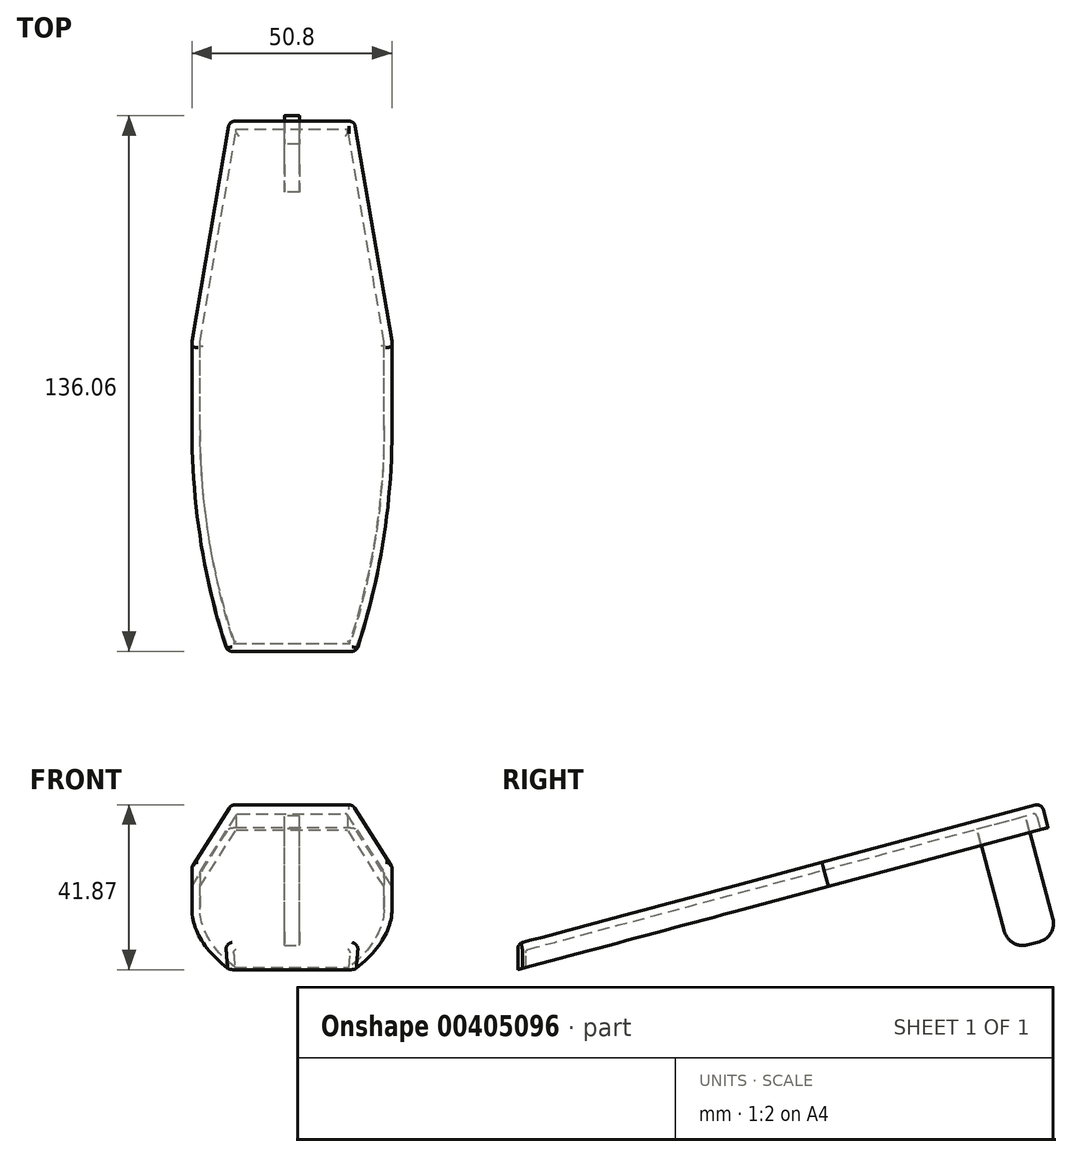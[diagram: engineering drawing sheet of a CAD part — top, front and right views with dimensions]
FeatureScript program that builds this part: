
annotation { "Feature Type Name" : "Feature", "Feature Type Description" : "" }
export const myFeature = defineFeature(function(context is Context, id is Id, definition is map)
    precondition{}
    {
        {
            var Q0;
            Q0=qCreatedBy(makeId("Right.planeOp"),FACE);
            var sketch = newSketch(context, id + "F0", { "sketchPlane" : qUnion([Q0])});
            skLineSegment(sketch, "E0", {"start": v(3.05, 2.38) * mm, "end": v(91.05, 71.15) * mm});
            skLineSegment(sketch, "E1", {"start": v(91.05, 71.15) * mm, "end": v(74.61, 132.48) * mm, "construction": true});
            skLineSegment(sketch, "E2", {"start": v(74.61, 132.48) * mm, "end": v(-60.33, 96.33) * mm});
            skLineSegment(sketch, "E3", {"start": v(-60.32, 96.33) * mm, "end": v(-60.33, -5.27) * mm});
            skLineSegment(sketch, "E4", {"start": v(-60.33, -5.27) * mm, "end": v(-7.85, -39.35) * mm});
            skLineSegment(sketch, "E5", {"start": v(0, -35.1) * mm, "end": v(0, -3.87) * mm});
            skPoint(sketch, "E6.visualSharp", {"position": v(0, 0) * mm});
            skArc(sketch, "E6.filletArc", {"start": v(3.05, 2.38) * mm, "mid": v(0.8, -0.4) * mm, "end": v(0, -3.87) * mm});
            skPoint(sketch, "E7.visualSharp", {"position": v(0, -44.45) * mm});
            skArc(sketch, "E7.filletArc", {"start": v(-7.85, -39.35) * mm, "mid": v(-2.66, -39.56) * mm, "end": v(0, -35.1) * mm});
            skArc(sketch, "E8", {"start": v(83.71, 98.52) * mm, "mid": v(82.28, 88.61) * mm, "end": v(88.48, 80.74) * mm});
            skCircle(sketch, "E9", {"center": v(69.86, 113.43) * mm, "radius": 3.18 * mm});
            skLineSegment(sketch, "E10", {"start": v(74.61, 132.48) * mm, "end": v(83.71, 98.52) * mm});
            skLineSegment(sketch, "E11", {"start": v(88.48, 80.74) * mm, "end": v(91.05, 71.15) * mm});
            skLineSegment(sketch, "E12", {"start": v(74.61, 132.48) * mm, "end": v(94.34, 58.88) * mm, "construction": true});
            skLineSegment(sketch, "E13", {"start": v(-60.33, 96.33) * mm, "end": v(-60.33, -44.45) * mm, "construction": true});
            skLineSegment(sketch, "E14", {"start": v(74.61, 132.48) * mm, "end": v(122.02, -44.45) * mm, "construction": true});
            skLineSegment(sketch, "E15", {"start": v(-60.33, -44.45) * mm, "end": v(122.02, -44.45) * mm, "construction": true});
            skSolve(sketch);
        }
        {
            var Q0;
            Q0=sQuery(id+"F0.wireOp",EDGE,"E2");
            cPlane(context, id + "F1", {"entities" : qUnion([Q0]), "cplaneType" : CPlaneType.LINE_ANGLE, "offset" : 25.4 * mm, "angle" : 0 * degree, "width" : 152.4 * mm, "height" : 152.4 * mm});
        }
        {
            var Q0;
            Q0=qCreatedBy(id+"F1.planeOp",FACE);
            var sketch = newSketch(context, id + "F2", { "sketchPlane" : qUnion([Q0])});
            skLineSegment(sketch, "E16.0", {"start": v(0, -106.36) * mm, "end": v(0, 33.34) * mm, "construction": true});
            skLineSegment(sketch, "E17", {"start": v(0, 33.34) * mm, "end": v(15.88, 33.34) * mm});
            skLineSegment(sketch, "E18", {"start": v(15.88, 33.34) * mm, "end": v(25.4, -26.15) * mm, "construction": true});
            skLineSegment(sketch, "E19", {"start": v(25.4, -26.15) * mm, "end": v(25.4, -48.6) * mm});
            skArc(sketch, "E20", {"start": v(25.4, -26.15) * mm, "mid": v(23, 3.98) * mm, "end": v(15.88, 33.34) * mm});
            skLineSegment(sketch, "E21", {"start": v(25.4, -48.6) * mm, "end": v(15.88, -106.36) * mm});
            skLineSegment(sketch, "E22", {"start": v(15.88, -106.36) * mm, "end": v(0, -106.36) * mm});
            skLineSegment(sketch, "E23.MirrorCS", {"start": v(0, 33.34) * mm, "end": v(-15.88, 33.34) * mm});
            skArc(sketch, "E24.MirrorCS", {"start": v(-25.4, -26.15) * mm, "mid": v(-23, 3.98) * mm, "end": v(-15.88, 33.34) * mm});
            skLineSegment(sketch, "E25.MirrorCS", {"start": v(-25.4, -26.15) * mm, "end": v(-25.4, -48.6) * mm});
            skLineSegment(sketch, "E26.MirrorCS", {"start": v(-25.4, -48.6) * mm, "end": v(-15.88, -106.36) * mm});
            skLineSegment(sketch, "E27.MirrorCS", {"start": v(-15.88, -106.36) * mm, "end": v(0, -106.36) * mm});
            skSolve(sketch);
        }
        {
            var Q0;
            Q0=makeQuery(id+"F2.imprint","IMPRINT",FACE,{"disambiguationData":[TD([[makeQuery(id+"F2.imprint","IMPRINT",EDGE,{"derivedFrom":sQuery(id+"F2.wireOp",EDGE,"E17")}),-1.0]])]});
            extrude(context, id + "F3", {"entities" : qUnion([Q0]), "oppositeDirection" : true, "depth" : 6.35 * mm, "offsetDistance" : 25.4 * mm});
        }
        {
            var Q0;
            Q0=qCreatedBy(makeId("Right.planeOp"),FACE);
            var sketch = newSketch(context, id + "F4", { "sketchPlane" : qUnion([Q0])});
            skLineSegment(sketch, "E28.0", {"start": v(-61.97, 102.46) * mm, "end": v(-60.33, 96.33) * mm});
            skLineSegment(sketch, "E28.1", {"start": v(-4.51, 117.85) * mm, "end": v(-61.97, 102.46) * mm, "construction": true});
            skLineSegment(sketch, "E29", {"start": v(-61.97, 102.46) * mm, "end": v(-60.08, 102.97) * mm});
            skLineSegment(sketch, "E30", {"start": v(-60.08, 102.97) * mm, "end": v(-60.08, 96.4) * mm});
            skLineSegment(sketch, "E31", {"start": v(-60.08, 96.4) * mm, "end": v(-60.33, 96.33) * mm});
            skSolve(sketch);
        }
        {
            var Q0;
            Q0 = qSketchRegion(id + "F4", true);
            extrude(context, id + "F5", {"entities" : qUnion([Q0]), "operationType" : NewBodyOperationType.REMOVE, "endBound" : BoundingType.THROUGH_ALL, "oppositeDirection" : true, "depth" : 25.4 * mm, "offsetDistance" : 25.4 * mm, "hasSecondDirection" : true, "secondDirectionBound" : SecondDirectionBoundingType.THROUGH_ALL, "secondDirectionOppositeDirection" : false, "secondDirectionDepth" : 25.4 * mm});
        }
        {
            var Q0;
            Q0=makeQuery(id+"F3.opExtrude","CAP_FACE",FACE,{"disambiguationData":[OSD([sQuery(id+"F2.wireOp",EDGE,"E17"),sQuery(id+"F2.wireOp",EDGE,"E19"),sQuery(id+"F2.wireOp",EDGE,"E20"),sQuery(id+"F2.wireOp",EDGE,"E21"),sQuery(id+"F2.wireOp",EDGE,"E22"),sQuery(id+"F2.wireOp",EDGE,"E23.MirrorCS"),sQuery(id+"F2.wireOp",EDGE,"E24.MirrorCS"),sQuery(id+"F2.wireOp",EDGE,"E25.MirrorCS"),sQuery(id+"F2.wireOp",EDGE,"E26.MirrorCS"),sQuery(id+"F2.wireOp",EDGE,"E27.MirrorCS")])],"isStart":true});
            shell(context, id + "F6", {"entities" : qUnion([Q0]), "thickness" : 2.03 * mm});
        }
        {
            var Q0;
            Q0=makeQuery(id+"F3.opExtrude","SWEPT_EDGE",EDGE,{"disambiguationData":[OSD([sQuery(id+"F2.wireOp",EDGE,"E17"),sQuery(id+"F2.wireOp",EDGE,"E20")])]});
            var Q1;
            Q1=makeQuery(id+"F3.opExtrude","SWEPT_EDGE",EDGE,{"disambiguationData":[OSD([sQuery(id+"F2.wireOp",EDGE,"E23.MirrorCS"),sQuery(id+"F2.wireOp",EDGE,"E24.MirrorCS")])]});
            var Q2;
            Q2=makeQuery(id+"F3.opExtrude","SWEPT_EDGE",EDGE,{"disambiguationData":[OSD([sQuery(id+"F2.wireOp",EDGE,"E21"),sQuery(id+"F2.wireOp",EDGE,"E22")])]});
            var Q3;
            Q3=makeQuery(id+"F3.opExtrude","SWEPT_EDGE",EDGE,{"disambiguationData":[OSD([sQuery(id+"F2.wireOp",EDGE,"E26.MirrorCS"),sQuery(id+"F2.wireOp",EDGE,"E27.MirrorCS")])]});
            var Q4;
            Q4=makeQuery(id+"F3.opExtrude","CAP_FACE",FACE,{"disambiguationData":[OSD([sQuery(id+"F2.wireOp",EDGE,"E17"),sQuery(id+"F2.wireOp",EDGE,"E19"),sQuery(id+"F2.wireOp",EDGE,"E20"),sQuery(id+"F2.wireOp",EDGE,"E21"),sQuery(id+"F2.wireOp",EDGE,"E22"),sQuery(id+"F2.wireOp",EDGE,"E23.MirrorCS"),sQuery(id+"F2.wireOp",EDGE,"E24.MirrorCS"),sQuery(id+"F2.wireOp",EDGE,"E25.MirrorCS"),sQuery(id+"F2.wireOp",EDGE,"E26.MirrorCS"),sQuery(id+"F2.wireOp",EDGE,"E27.MirrorCS")])],"isStart":false});
            var Q5;
            Q5=makeQuery(id+"F5.boolean.opBoolean","INTERSECT",EDGE,{"derivedFrom":[makeQuery(id+"F3.opExtrude","SWEPT_FACE",FACE,{"disambiguationData":[OSD([sQuery(id+"F2.wireOp",EDGE,"E20")])]}),makeQuery(id+"F5.opExtrude","SWEPT_FACE",FACE,{"disambiguationData":[OSD([sQuery(id+"F4.wireOp",EDGE,"E30")])]})]});
            var Q6;
            Q6=makeQuery(id+"F5.boolean.opBoolean","INTERSECT",EDGE,{"derivedFrom":[makeQuery(id+"F3.opExtrude","SWEPT_FACE",FACE,{"disambiguationData":[OSD([sQuery(id+"F2.wireOp",EDGE,"E24.MirrorCS")])]}),makeQuery(id+"F5.opExtrude","SWEPT_FACE",FACE,{"disambiguationData":[OSD([sQuery(id+"F4.wireOp",EDGE,"E30")])]})]});
            fillet(context, id + "F7", {"entities" : qUnion([Q0, Q1, Q2, Q3, Q4, Q5, Q6]), "tangentPropagation" : true, "radius" : 1.59 * mm, "defaultsChanged" : false, "vertexSettings" : [], "allowEdgeOverflow" : false});
        }
        {
            var Q0;
            Q0=makeQuery(id+"F10.opExtrude","SWEPT_EDGE",EDGE,{"disambiguationData":[OSD([sQuery(id+"F9.wireOp",EDGE,"E32.top"),sQuery(id+"F9.wireOp",EDGE,"E32.left")])]});
            var Q1;
            Q1=makeQuery(id+"F10.opExtrude","SWEPT_EDGE",EDGE,{"disambiguationData":[OSD([sQuery(id+"F9.wireOp",EDGE,"E32.top"),sQuery(id+"F9.wireOp",EDGE,"E32.right")])]});
            var Q2;
            Q2=makeQuery(id+"F6.opShell","OFFSET_FACE",FACE,{"disambiguationData":[OSD([sQuery(id+"F2.wireOp",EDGE,"E17"),sQuery(id+"F2.wireOp",EDGE,"E19"),sQuery(id+"F2.wireOp",EDGE,"E20"),sQuery(id+"F2.wireOp",EDGE,"E21"),sQuery(id+"F2.wireOp",EDGE,"E22"),sQuery(id+"F2.wireOp",EDGE,"E23.MirrorCS"),sQuery(id+"F2.wireOp",EDGE,"E24.MirrorCS"),sQuery(id+"F2.wireOp",EDGE,"E25.MirrorCS"),sQuery(id+"F2.wireOp",EDGE,"E26.MirrorCS"),sQuery(id+"F2.wireOp",EDGE,"E27.MirrorCS")])]});
            fillet(context, id + "F8", {"entities" : qUnion([Q0, Q1, Q2]), "tangentPropagation" : true, "radius" : 0.76 * mm, "defaultsChanged" : false, "vertexSettings" : [], "allowEdgeOverflow" : false});
        }
        {
            var Q0;
            Q0=makeQuery(id+"F6.opShell","OFFSET_FACE",FACE,{"disambiguationData":[OSD([sQuery(id+"F2.wireOp",EDGE,"E17"),sQuery(id+"F2.wireOp",EDGE,"E19"),sQuery(id+"F2.wireOp",EDGE,"E20"),sQuery(id+"F2.wireOp",EDGE,"E21"),sQuery(id+"F2.wireOp",EDGE,"E22"),sQuery(id+"F2.wireOp",EDGE,"E23.MirrorCS"),sQuery(id+"F2.wireOp",EDGE,"E24.MirrorCS"),sQuery(id+"F2.wireOp",EDGE,"E25.MirrorCS"),sQuery(id+"F2.wireOp",EDGE,"E26.MirrorCS"),sQuery(id+"F2.wireOp",EDGE,"E27.MirrorCS")])]});
            var sketch = newSketch(context, id + "F9", { "sketchPlane" : qUnion([Q0])});
            skLineSegment(sketch, "E32.bottom", {"start": v(1.9, -88.84) * mm, "end": v(-1.9, -88.84) * mm});
            skLineSegment(sketch, "E32.top", {"start": v(1.9, -101.54) * mm, "end": v(-1.9, -101.54) * mm});
            skLineSegment(sketch, "E32.left", {"start": v(1.9, -88.84) * mm, "end": v(1.9, -101.54) * mm});
            skLineSegment(sketch, "E32.right", {"start": v(-1.9, -88.84) * mm, "end": v(-1.9, -101.54) * mm});
            skPoint(sketch, "E32.middle", {"position": v(0, -95.19) * mm});
            skLineSegment(sketch, "E33.0", {"start": v(14.15, -104.33) * mm, "end": v(-14.15, -104.33) * mm, "construction": true});
            skSolve(sketch);
        }
        {
            var Q0;
            Q0=makeQuery(id+"F9.imprint","IMPRINT",FACE,{"disambiguationData":[TD([[makeQuery(id+"F9.imprint","IMPRINT",EDGE,{"derivedFrom":sQuery(id+"F9.wireOp",EDGE,"E32.bottom")}),1.0]])]});
            extrude(context, id + "F10", {"entities" : qUnion([Q0]), "operationType" : NewBodyOperationType.ADD, "depth" : 31.75 * mm, "offsetDistance" : 25.4 * mm});
        }
        {
            var Q0;
            Q0=makeQuery(id+"F10.opExtrude","CAP_EDGE",EDGE,{"disambiguationData":[OSD([sQuery(id+"F9.wireOp",EDGE,"E32.top")])],"isStart":false});
            var Q1;
            Q1=makeQuery(id+"F10.opExtrude","CAP_EDGE",EDGE,{"disambiguationData":[OSD([sQuery(id+"F9.wireOp",EDGE,"E32.bottom")])],"isStart":false});
            var Q2;
            Q2=makeQuery(id+"F10.opExtrude","CAP_EDGE",EDGE,{"disambiguationData":[OSD([sQuery(id+"F9.wireOp",EDGE,"E32.right")])],"isStart":true});
            var Q3;
            Q3=makeQuery(id+"F10.opExtrude","CAP_EDGE",EDGE,{"disambiguationData":[OSD([sQuery(id+"F9.wireOp",EDGE,"E32.left")])],"isStart":true});
            var Q4;
            Q4=makeQuery(id+"F10.opExtrude","CAP_EDGE",EDGE,{"disambiguationData":[OSD([sQuery(id+"F9.wireOp",EDGE,"E32.bottom")])],"isStart":true});
            fillet(context, id + "F11", {"entities" : qUnion([Q0, Q1, Q2, Q3, Q4]), "tangentPropagation" : true, "radius" : 4.76 * mm, "defaultsChanged" : false, "vertexSettings" : [], "allowEdgeOverflow" : false});
        }
    });
